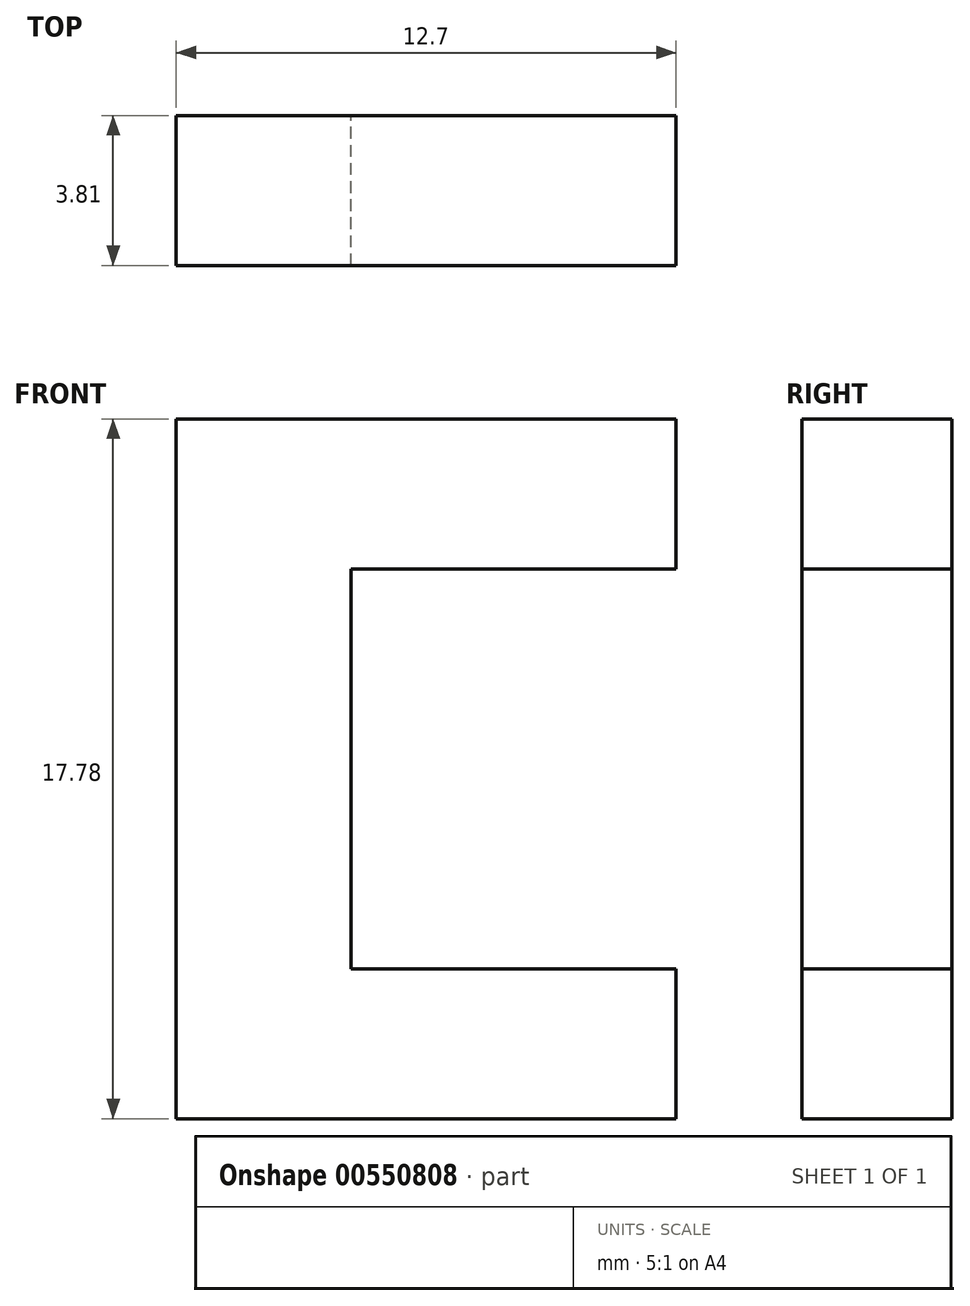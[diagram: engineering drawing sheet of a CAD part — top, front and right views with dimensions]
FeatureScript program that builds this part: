
annotation { "Feature Type Name" : "Feature", "Feature Type Description" : "" }
export const myFeature = defineFeature(function(context is Context, id is Id, definition is map)
    precondition{}
    {
        {
            var Q0;
            Q0=qCreatedBy(makeId("Front.planeOp"),FACE);
            var sketch = newSketch(context, id + "F0", { "sketchPlane" : qUnion([Q0])});
            skLineSegment(sketch, "E0", {"start": v(0, 0) * mm, "end": v(-12.7, 0) * mm});
            skLineSegment(sketch, "E1", {"start": v(-12.7, 0) * mm, "end": v(-12.7, 17.78) * mm});
            skLineSegment(sketch, "E2", {"start": v(-12.7, 17.78) * mm, "end": v(0, 17.78) * mm});
            skLineSegment(sketch, "E3", {"start": v(0, 17.78) * mm, "end": v(0, 13.97) * mm});
            skLineSegment(sketch, "E4", {"start": v(0, 13.97) * mm, "end": v(-8.26, 13.97) * mm});
            skLineSegment(sketch, "E5", {"start": v(-8.26, 13.97) * mm, "end": v(-8.26, 3.8) * mm});
            skLineSegment(sketch, "E6", {"start": v(-8.26, 3.81) * mm, "end": v(0, 3.81) * mm});
            skLineSegment(sketch, "E7", {"start": v(0, 3.81) * mm, "end": v(0, 0) * mm});
            skSolve(sketch);
        }
        {
            var Q0;
            Q0 = qSketchRegion(id + "F0", true);
            extrude(context, id + "F1", {"entities" : qUnion([Q0]), "depth" : 3.8 * mm, "offsetDistance" : 25.4 * mm});
        }
    });
